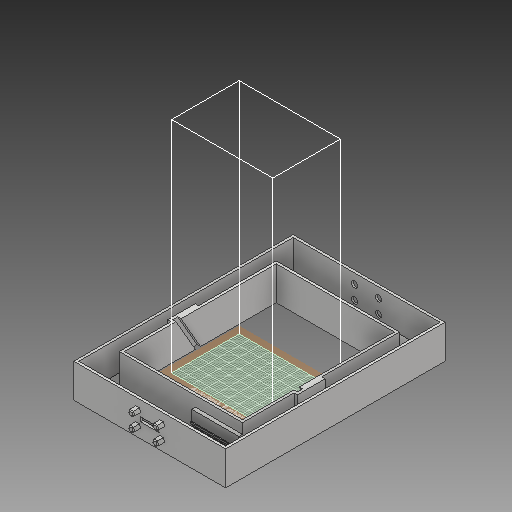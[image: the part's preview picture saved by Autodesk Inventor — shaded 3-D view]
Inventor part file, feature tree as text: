
AUTODESK INVENTOR PART (.ipt)
format: ipt  version: 2018.3 (Build 223284000, 284)  size: 666,112 bytes
history: native  units: mm
features: extrude x14, sketch x14, chamfer x3
ambient origin geometry x8: Origin, YZ Plane, XZ Plane, XY Plane, X Axis, Y Axis, Z Axis, Center Point
bodies: Solid1 (feature_tree)
feature tree (31):
  extrude  "Extrusion1"  Depth=130.0mm
  extrude  "Extrusion2"  Depth=90.0mm
  extrude  "Extrusion3"  TaperAngle=210.0deg  [1 undecoded]
  extrude  "Extrusion4"  Depth=2.0mm
  chamfer  "Chamfer1"  Distance=2.0mm
  extrude  "Extrusion5"  Depth=3.0mm
  chamfer  "Chamfer2"  Distance=2.0mm
  extrude  "Extrusion6"  Depth=20.0mm
  extrude  "Extrusion7"  Depth=20.0mm
  extrude  "Extrusion8"  Depth=3.0mm
  extrude  "Extrusion9"  Depth=35.0mm
  extrude  "Extrusion10"  Depth=35.0mm
  extrude  "Extrusion11"  Depth=1.1mm
  extrude  "Extrusion12"  Depth=12.11mm
  extrude  "Extrusion13"  Depth=2.0mm
  extrude  "Extrusion14"  Depth=2.0mm
  chamfer  "Chamfer3"  Distance=4.83mm
  sketch  "Sketch1"  dims[d0=90.0mm d1=130.0mm]
  sketch  "Sketch2"  dims[d2=70.0mm d3=90.0mm]
  sketch  "Sketch3"  dims[d4=20.0mm d5=0.0mm d6=210.0deg]
  sketch  "Sketch4"  dims[d7=3.0mm d8=26.471143mm d9=2.0mm d10=0.0mm]
  sketch  "Sketch5"  dims[d11=30.0deg d12=3.0mm]
  sketch  "Sketch6"  dims[d13=26.471143mm d14=2.0mm d15=0.0mm]
  sketch  "Sketch7"  dims[d16=20.0mm d17=20.0mm]
  sketch  "Sketch8"  dims[d18=10.0mm d19=20.0mm]
  sketch  "Sketch9"  dims[d20=14.0mm d21=3.0mm]
  sketch  "Sketch10"  dims[d22=3.0mm d23=35.0mm]
  sketch  "Sketch11"  dims[d24=35.0mm d25=1.45mm]
  sketch  "Sketch12"  dims[d26=1.45mm d27=1.1mm]
  sketch  "Sketch13"  dims[d28=1.1mm d29=12.11mm]
  sketch  "Sketch14"  dims[d30=1.13mm d31=1.13mm d32=4.83mm d33=4.83mm d34=1.129mm d35=1.128692mm d36=4.0mm d37=0.0mm d38=0.5mm d39=2.0mm d40=45.0deg d41=20.0mm d42=14.0mm d43=3.0mm d44=3.0mm d45=35.0mm d46=35.0mm d74=4.0mm d75=0.0mm d76=0.5mm d77=2.0mm d78=45.0deg d79=128.5mm d80=87.0mm d81=127.0mm d82=46.0mm d83=2.0mm d84=16.434mm d85=2.0mm d86=30.566mm d87=73.0mm d88=2.0mm d89=18.0mm d90=0.0mm d100=11.0mm d101=2.6mm d102=8.7mm d103=39.5mm d104=39.5mm d105=8.7mm d106=10.0mm d107=0.0mm d108=28.0mm d109=6.0mm d110=2.2mm d111=0.0mm d114=28.0mm d115=12.0mm d116=7.0mm d117=2.2mm d118=0.0mm d119=1.0mm d120=0.0mm d121=8.8mm d122=1.0mm d123=6.0mm d124=0.55mm d125=0.0mm d126=0.6mm d127=0.0mm d128=1.0mm d129=1.0mm d130=6.2mm d131=1.8mm d132=0.55mm d133=0.0mm d134=0.6mm d135=0.0mm d136=7.0mm d137=0.0mm d138=6.0mm d139=2.0mm d140=1.745329mm d141=1.45mm d142=2.15mm d143=1.13mm d144=2.15mm d145=1.13mm d146=1.1mm d148=2.15mm d149=1.1mm d150=1.128mm d151=4.83298mm d153=12.113227mm d154=2.15mm d155=1.128mm d156=1.45mm d157=4.83298mm d158=12.113227mm]
note: 1 required parameter value undecoded (feature->parameter linkage not recoverable at this tier; creation-order binding heuristic only, values carry confidence <= 0.55)
